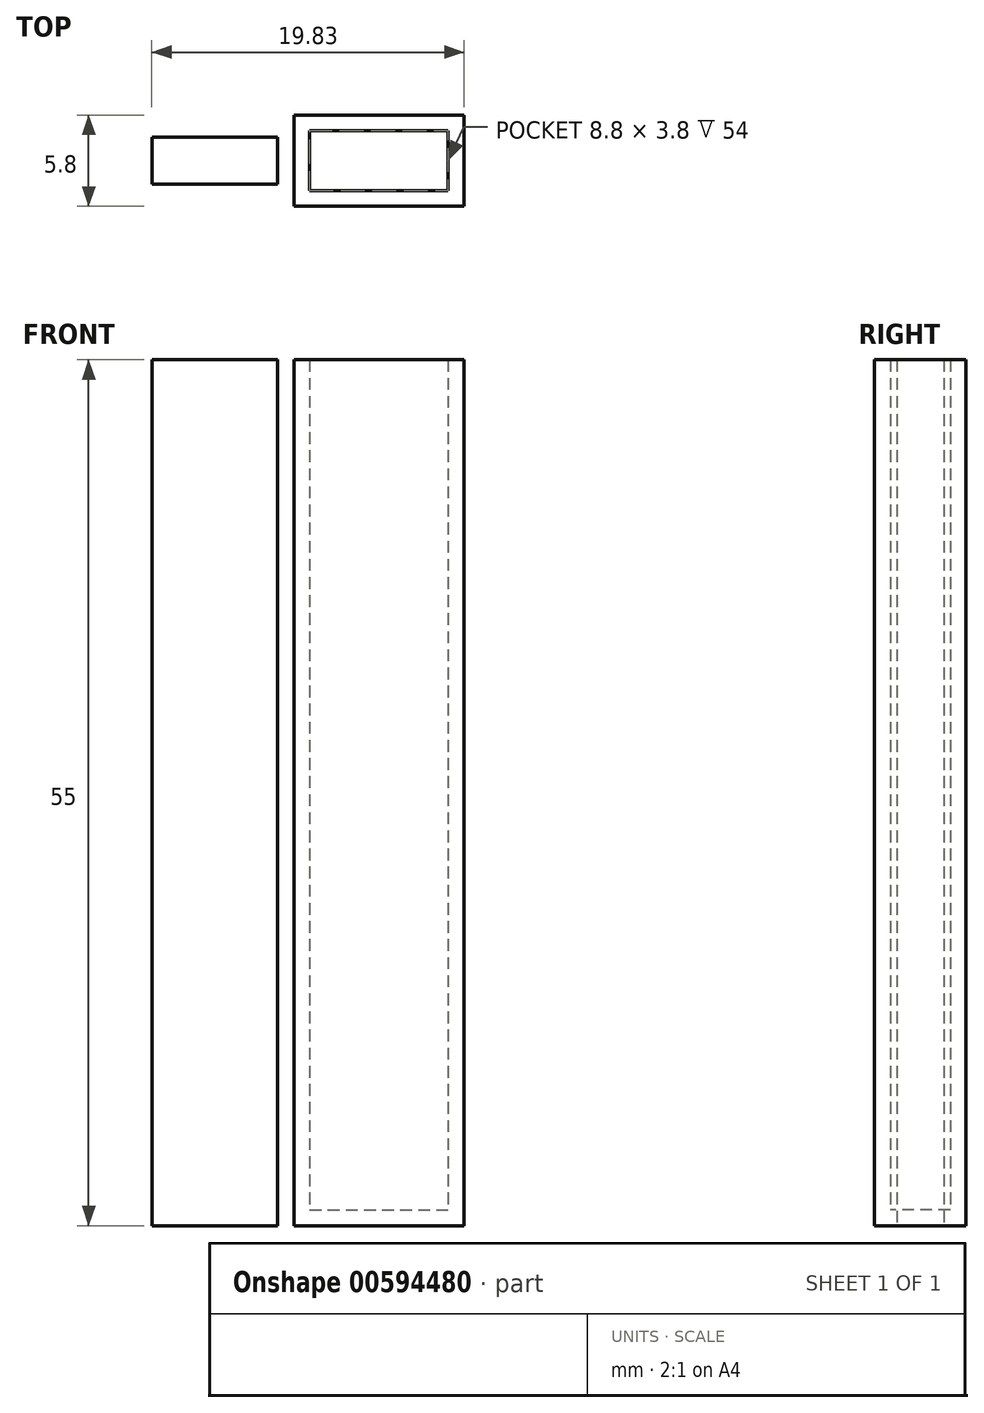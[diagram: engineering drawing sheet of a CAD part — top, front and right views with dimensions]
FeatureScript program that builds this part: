
annotation { "Feature Type Name" : "Feature", "Feature Type Description" : "" }
export const myFeature = defineFeature(function(context is Context, id is Id, definition is map)
    precondition{}
    {
        {
            var Q0;
            Q0=qCreatedBy(makeId("Top.planeOp"),FACE);
            var sketch = newSketch(context, id + "F0", { "sketchPlane" : qUnion([Q0])});
            skLineSegment(sketch, "E0.bottom", {"start": v(-11.53, 0) * mm, "end": v(-3.53, 0) * mm});
            skLineSegment(sketch, "E0.top", {"start": v(-11.53, 3) * mm, "end": v(-3.53, 3) * mm});
            skLineSegment(sketch, "E0.left", {"start": v(-11.53, 0) * mm, "end": v(-11.53, 3) * mm});
            skLineSegment(sketch, "E0.right", {"start": v(-3.53, 0) * mm, "end": v(-3.53, 3) * mm});
            skLineSegment(sketch, "E1.bottom", {"start": v(-1.1, 3) * mm, "end": v(6.9, 3) * mm, "construction": true});
            skLineSegment(sketch, "E1.top", {"start": v(-1.1, 0) * mm, "end": v(6.9, 0) * mm, "construction": true});
            skLineSegment(sketch, "E1.left", {"start": v(-1.1, 3) * mm, "end": v(-1.1, 0) * mm, "construction": true});
            skLineSegment(sketch, "E1.right", {"start": v(6.9, 3) * mm, "end": v(6.9, 0) * mm, "construction": true});
            skLineSegment(sketch, "E2.0", {"start": v(-2.5, -1.4) * mm, "end": v(8.3, -1.4) * mm});
            skLineSegment(sketch, "E2.1", {"start": v(-2.5, 4.4) * mm, "end": v(-2.5, -1.4) * mm});
            skLineSegment(sketch, "E2.2", {"start": v(-2.5, 4.4) * mm, "end": v(8.3, 4.4) * mm});
            skLineSegment(sketch, "E2.3", {"start": v(8.3, 4.4) * mm, "end": v(8.3, -1.4) * mm});
            skSolve(sketch);
        }
        {
            var Q0;
            Q0=qSketchRegion(id+"F0",true);
            var Q1;
            Q1=sQuery(id+"F0.wireOp",EDGE,"nauhSgGS-zy9I-HaWY-opW2-mhqk7vYS6UTa.right");
            var Q2;
            Q2=sQuery(id+"F0.wireOp",EDGE,"nauhSgGS-zy9I-HaWY-opW2-mhqk7vYS6UTa.top");
            var Q3;
            Q3=sQuery(id+"F0.wireOp",EDGE,"nauhSgGS-zy9I-HaWY-opW2-mhqk7vYS6UTa.left");
            var Q4;
            Q4=sQuery(id+"F0.wireOp",EDGE,"nauhSgGS-zy9I-HaWY-opW2-mhqk7vYS6UTa.bottom");
            extrude(context, id + "F1", {"entities" : qUnion([Q0]), "surfaceEntities" : qUnion([Q1, Q2, Q3, Q4]), "depth" : 55 * mm});
        }
        {
            var Q0;
            Q0=makeQuery(id+"F1.opExtrude","CAP_FACE",FACE,{"disambiguationData":[OSD([sQuery(id+"F0.wireOp",EDGE,"E2.0"),sQuery(id+"F0.wireOp",EDGE,"E2.1"),sQuery(id+"F0.wireOp",EDGE,"E2.2"),sQuery(id+"F0.wireOp",EDGE,"E2.3")])],"isStart":false});
            shell(context, id + "F2", {"entities" : qUnion([Q0]), "thickness" : 1 * mm});
        }
    });
